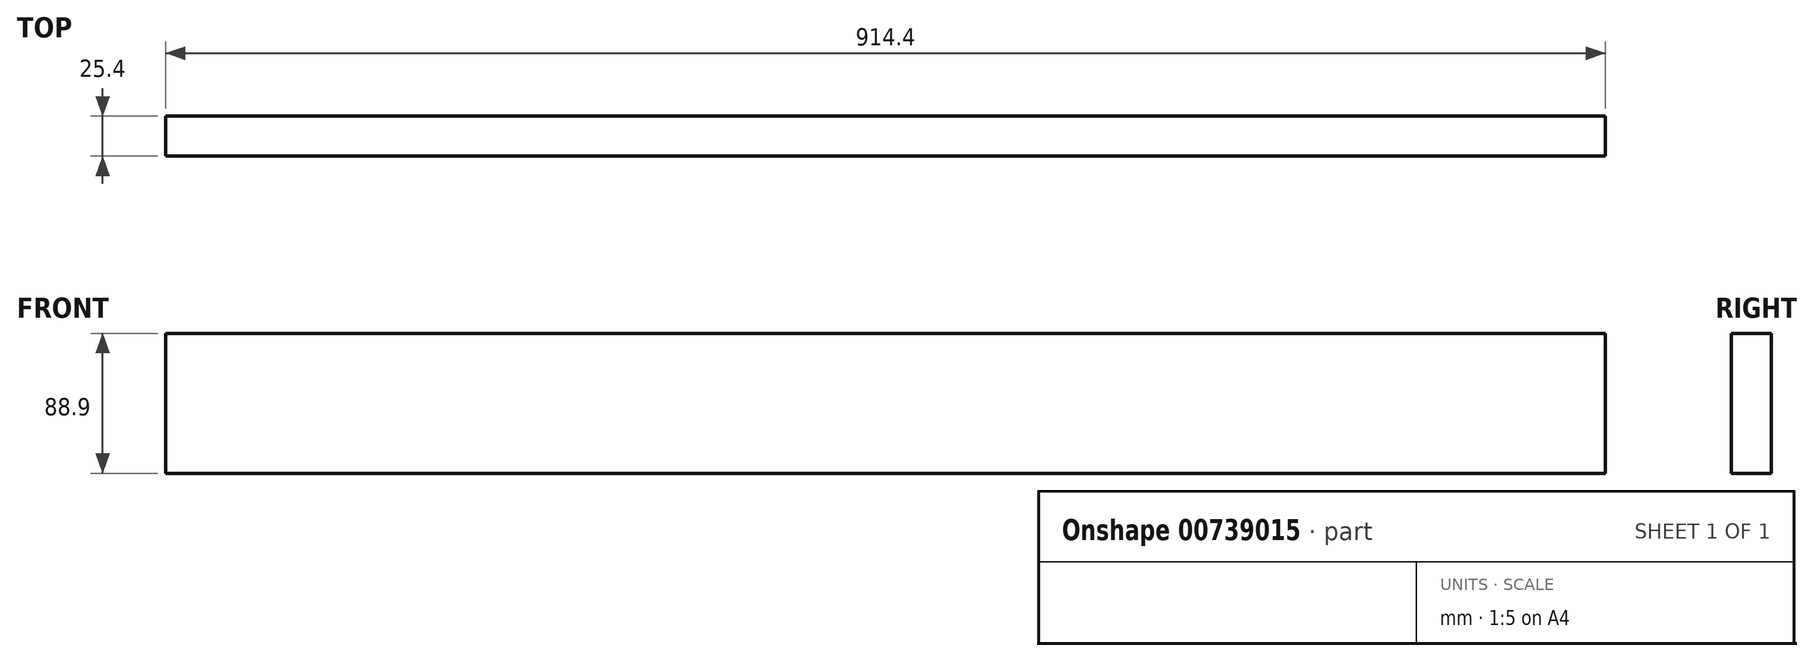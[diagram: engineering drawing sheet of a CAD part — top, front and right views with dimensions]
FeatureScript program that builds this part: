
annotation { "Feature Type Name" : "Feature", "Feature Type Description" : "" }
export const myFeature = defineFeature(function(context is Context, id is Id, definition is map)
    precondition{}
    {
        {
            var Q0;
            Q0=qCreatedBy(makeId("Front.planeOp"),FACE);
            var sketch = newSketch(context, id + "F0", { "sketchPlane" : qUnion([Q0])});
            skLineSegment(sketch, "E0.bottom", {"start": v(-531.37, -51.7) * mm, "end": v(383.03, -51.7) * mm});
            skLineSegment(sketch, "E0.top", {"start": v(-531.37, -140.6) * mm, "end": v(383.03, -140.6) * mm});
            skLineSegment(sketch, "E0.left", {"start": v(-531.37, -51.7) * mm, "end": v(-531.37, -140.6) * mm});
            skLineSegment(sketch, "E0.right", {"start": v(383.03, -51.7) * mm, "end": v(383.03, -140.6) * mm});
            skSolve(sketch);
        }
        {
            var Q0;
            Q0 = qSketchRegion(id + "F0", true);
            extrude(context, id + "F1", {"entities" : qUnion([Q0]), "depth" : 25.4 * mm, "offsetDistance" : 25.4 * mm});
        }
    });
